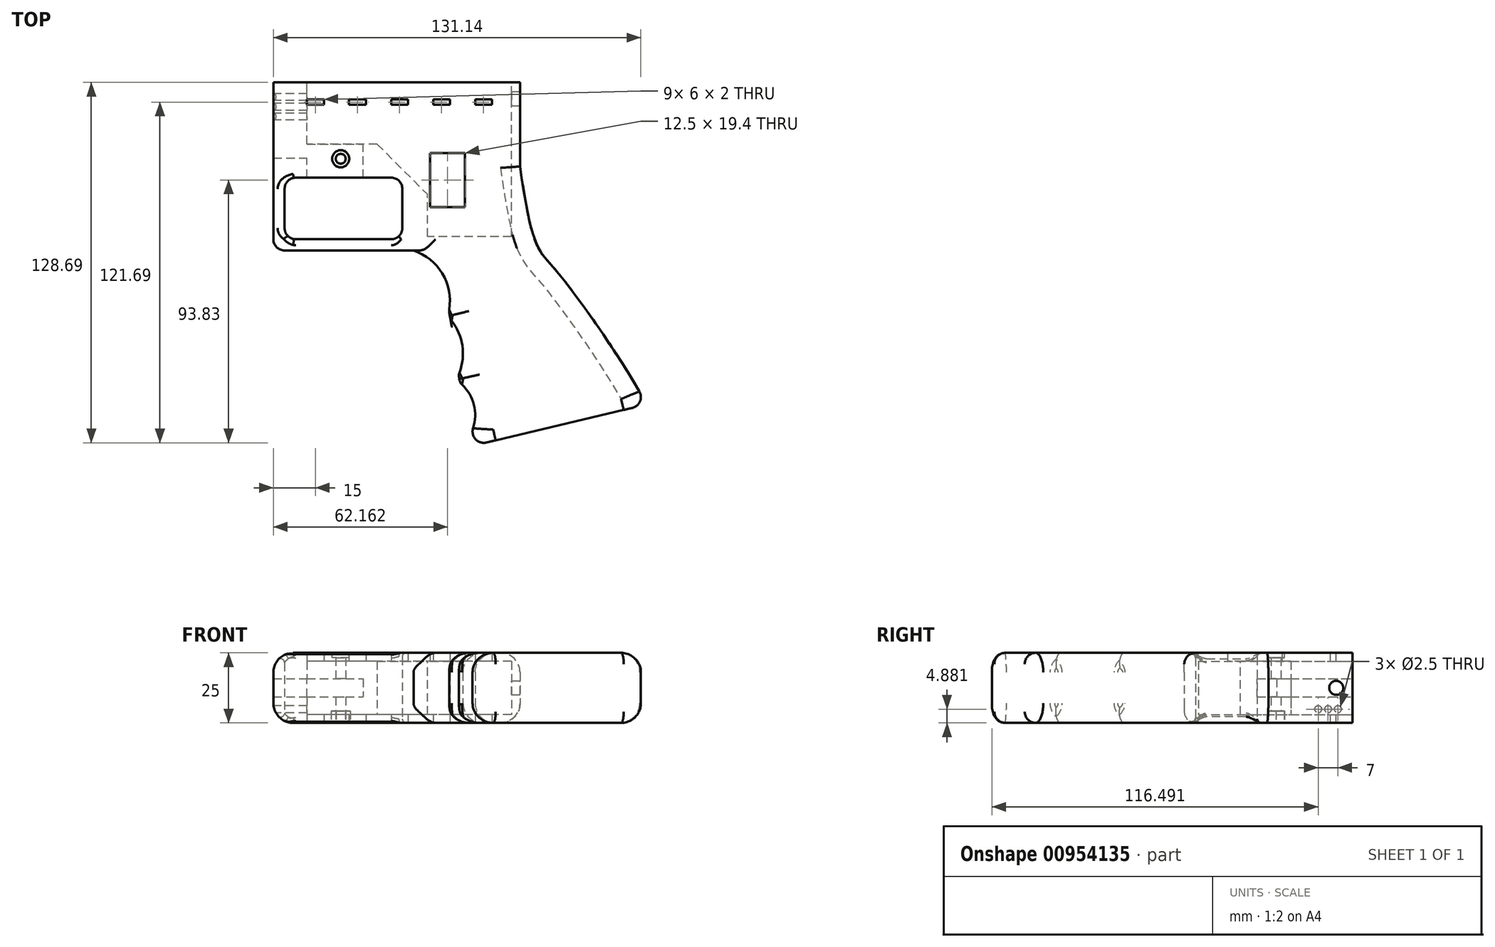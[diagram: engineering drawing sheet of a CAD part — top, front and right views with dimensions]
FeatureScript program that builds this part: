
annotation { "Feature Type Name" : "Feature", "Feature Type Description" : "" }
export const myFeature = defineFeature(function(context is Context, id is Id, definition is map)
    precondition{}
    {
        {
            var Q0;
            Q0=qCreatedBy(makeId("Top.planeOp"),FACE);
            var sketch = newSketch(context, id + "F0", { "sketchPlane" : qUnion([Q0])});
            skLineSegment(sketch, "E0.bottom", {"start": v(44, 30) * mm, "end": v(-44, 30) * mm});
            skLineSegment(sketch, "E0.top", {"start": v(44, -30) * mm, "end": v(-44, -30) * mm});
            skLineSegment(sketch, "E0.left", {"start": v(44, 30) * mm, "end": v(44, -30) * mm});
            skLineSegment(sketch, "E0.right", {"start": v(-44, 30) * mm, "end": v(-44, -30) * mm});
            skPoint(sketch, "E0.middle", {"position": v(0, 0) * mm});
            skLineSegment(sketch, "E1.bottom", {"start": v(-40, -4) * mm, "end": v(2, -4) * mm});
            skLineSegment(sketch, "E1.top", {"start": v(-40, -26) * mm, "end": v(2, -26) * mm});
            skLineSegment(sketch, "E1.left", {"start": v(-40, -4) * mm, "end": v(-40, -26) * mm});
            skLineSegment(sketch, "E1.right", {"start": v(2, -4) * mm, "end": v(2, -26) * mm});
            skLineSegment(sketch, "E2.bottom", {"start": v(-32, 24) * mm, "end": v(-26, 24) * mm});
            skLineSegment(sketch, "E2.top", {"start": v(-32, 22) * mm, "end": v(-26, 22) * mm});
            skLineSegment(sketch, "E2.left", {"start": v(-32, 24) * mm, "end": v(-32, 22) * mm});
            skLineSegment(sketch, "E2.right", {"start": v(-26, 24) * mm, "end": v(-26, 22) * mm});
            skLineSegment(sketch, "E3.1.0.0", {"start": v(-17, 24) * mm, "end": v(-11, 24) * mm});
            skLineSegment(sketch, "E3.1.0.1", {"start": v(-11, 24) * mm, "end": v(-11, 22) * mm});
            skLineSegment(sketch, "E3.1.0.2", {"start": v(-17, 22) * mm, "end": v(-11, 22) * mm});
            skLineSegment(sketch, "E3.1.0.3", {"start": v(-17, 24) * mm, "end": v(-17, 22) * mm});
            skLineSegment(sketch, "E3.2.0.0", {"start": v(-2, 24) * mm, "end": v(4, 24) * mm});
            skLineSegment(sketch, "E3.2.0.1", {"start": v(4, 24) * mm, "end": v(4, 22) * mm});
            skLineSegment(sketch, "E3.2.0.2", {"start": v(-2, 22) * mm, "end": v(4, 22) * mm});
            skLineSegment(sketch, "E3.2.0.3", {"start": v(-2, 24) * mm, "end": v(-2, 22) * mm});
            skLineSegment(sketch, "E3.direction1", {"start": v(-32, 24) * mm, "end": v(-17, 24) * mm, "construction": true});
            skLineSegment(sketch, "E4.0.3.0", {"start": v(13, 24) * mm, "end": v(19, 24) * mm});
            skLineSegment(sketch, "E4.3.3.0", {"start": v(19, 24) * mm, "end": v(19, 22) * mm});
            skLineSegment(sketch, "E4.6.3.0", {"start": v(13, 22) * mm, "end": v(19, 22) * mm});
            skLineSegment(sketch, "E4.9.3.0", {"start": v(13, 24) * mm, "end": v(13, 22) * mm});
            skLineSegment(sketch, "E4.0.4.0", {"start": v(28, 24) * mm, "end": v(34, 24) * mm});
            skLineSegment(sketch, "E4.3.4.0", {"start": v(34, 24) * mm, "end": v(34, 22) * mm});
            skLineSegment(sketch, "E4.6.4.0", {"start": v(28, 22) * mm, "end": v(34, 22) * mm});
            skLineSegment(sketch, "E4.9.4.0", {"start": v(28, 24) * mm, "end": v(28, 22) * mm});
            skFitSpline(sketch, "E5", {"points": [v(44, 0) * mm, v(56.7, -36.96) * mm, v(89.25, -85) * mm], "startDerivative": vector(29.34, -199.67) * mm, "endDerivative": vector(48.39, -88.32) * mm});
            skLineSegment(sketch, "E6", {"start": v(89.25, -85) * mm, "end": v(26, -100) * mm});
            skLineSegment(sketch, "E7", {"start": v(26, -100) * mm, "end": v(25.55, -97.03) * mm});
            skArc(sketch, "E8", {"start": v(18.67, -51.55) * mm, "mid": v(16.38, -38.4) * mm, "end": v(6, -30) * mm});
            skArc(sketch, "E9", {"start": v(22.11, -74.3) * mm, "mid": v(23.43, -63.98) * mm, "end": v(19.12, -54.52) * mm});
            skArc(sketch, "E10", {"start": v(25.55, -97.03) * mm, "mid": v(27.83, -86.57) * mm, "end": v(22.56, -77.26) * mm});
            skLineSegment(sketch, "E11.trimOffspring", {"start": v(19.12, -54.52) * mm, "end": v(18.67, -51.55) * mm});
            skLineSegment(sketch, "E12.trimOffspring", {"start": v(22.56, -77.26) * mm, "end": v(22.11, -74.3) * mm});
            skSolve(sketch);
        }
        {
            var Q0;
            {var subQ1=sQuery(id+"F0.wireOp",EDGE,"E0.bottom");Q0=makeQuery(id+"F0.imprint","IMPRINT",FACE,{"disambiguationData":[TD([[makeQuery(id+"F0.imprint","IMPRINT",EDGE,{"derivedFrom":subQ1}),1.0]])]});}
            var Q1;
            {var subQ0=sQuery(id+"F0.wireOp",EDGE,"E5");Q1=makeQuery(id+"F0.imprint","IMPRINT",FACE,{"disambiguationData":[TD([[makeQuery(id+"F0.imprint","IMPRINT",EDGE,{"derivedFrom":subQ0}),-1.0]])]});}
            extrude(context, id + "F1", {"entities" : qUnion([Q0, Q1]), "depth" : 25 * mm, "offsetDistance" : 25 * mm});
        }
        {
            var Q0;
            Q0=makeQuery(id+"F1.opExtrude","SWEPT_FACE",FACE,{"disambiguationData":[OSD([sQuery(id+"F0.wireOp",EDGE,"E0.bottom")])]});
            var sketch = newSketch(context, id + "F2", { "sketchPlane" : qUnion([Q0])});
            skLineSegment(sketch, "E13.bottom", {"start": v(-41, 22) * mm, "end": v(32, 22) * mm});
            skLineSegment(sketch, "E13.top", {"start": v(-41, 3) * mm, "end": v(32, 3) * mm});
            skLineSegment(sketch, "E13.left", {"start": v(-41, 22) * mm, "end": v(-41, 3) * mm});
            skLineSegment(sketch, "E13.right", {"start": v(32, 22) * mm, "end": v(32, 3) * mm});
            skLineSegment(sketch, "E14", {"start": v(-11, 22) * mm, "end": v(-11, 3) * mm});
            skLineSegment(sketch, "E15.bottom", {"start": v(44, 15.75) * mm, "end": v(12, 15.75) * mm});
            skLineSegment(sketch, "E15.top", {"start": v(44, 9.25) * mm, "end": v(12, 9.25) * mm});
            skLineSegment(sketch, "E15.left", {"start": v(44, 15.75) * mm, "end": v(44, 9.25) * mm});
            skLineSegment(sketch, "E15.right", {"start": v(12, 15.75) * mm, "end": v(12, 9.25) * mm});
            skLineSegment(sketch, "E16", {"start": v(16.73, 22) * mm, "end": v(16.73, 15.75) * mm, "construction": true});
            skLineSegment(sketch, "E17", {"start": v(16.98, 9.25) * mm, "end": v(16.98, 3) * mm, "construction": true});
            skSolve(sketch);
        }
        {
            var Q0;
            {var subQ0=sQuery(id+"F2.wireOp",EDGE,"E13.left");Q0=makeQuery(id+"F2.imprint","IMPRINT",FACE,{"disambiguationData":[TD([[makeQuery(id+"F2.imprint","IMPRINT",EDGE,{"derivedFrom":subQ0}),1.0]])]});}
            var Q1;
            {var subQ9=sQuery(id+"F2.wireOp",EDGE,"E14");Q1=makeQuery(id+"F2.imprint","IMPRINT",FACE,{"disambiguationData":[TD([[makeQuery(id+"F2.imprint","IMPRINT",EDGE,{"derivedFrom":subQ9}),1.0]])]});}
            var Q2;
            {var subQ5=sQuery(id+"F2.wireOp",EDGE,"E15.left");Q2=makeQuery(id+"F2.imprint","IMPRINT",FACE,{"disambiguationData":[TD([[makeQuery(id+"F2.imprint","IMPRINT",EDGE,{"derivedFrom":subQ5}),-1.0]])]});}
            var Q3;
            {var subQ5=sQuery(id+"F2.wireOp",EDGE,"E15.right");Q3=makeQuery(id+"F2.imprint","IMPRINT",FACE,{"disambiguationData":[TD([[makeQuery(id+"F2.imprint","IMPRINT",EDGE,{"derivedFrom":subQ5}),1.0]])]});}
            extrude(context, id + "F3", {"entities" : qUnion([Q0, Q1, Q2, Q3]), "operationType" : NewBodyOperationType.REMOVE, "oppositeDirection" : true, "depth" : 22 * mm, "offsetDistance" : 25 * mm});
        }
        {
            var Q0;
            {var subQ0=sQuery(id+"F2.wireOp",EDGE,"E13.left");Q0=makeQuery(id+"F2.imprint","IMPRINT",FACE,{"disambiguationData":[TD([[makeQuery(id+"F2.imprint","IMPRINT",EDGE,{"derivedFrom":subQ0}),1.0]])]});}
            extrude(context, id + "F4", {"entities" : qUnion([Q0]), "operationType" : NewBodyOperationType.REMOVE, "oppositeDirection" : true, "depth" : 55 * mm, "offsetDistance" : 25 * mm});
        }
        {
            var Q0;
            {var subQ5=sQuery(id+"F2.wireOp",EDGE,"E15.right");Q0=makeQuery(id+"F2.imprint","IMPRINT",FACE,{"disambiguationData":[TD([[makeQuery(id+"F2.imprint","IMPRINT",EDGE,{"derivedFrom":subQ5}),1.0]])]});}
            var Q1;
            Q1=makeQuery(id+"F1.opExtrude","SWEPT_FACE",FACE,{"disambiguationData":[OSD([sQuery(id+"F0.wireOp",EDGE,"E1.bottom")])]});
            extrude(context, id + "F5", {"entities" : qUnion([Q0]), "operationType" : NewBodyOperationType.REMOVE, "endBound" : BoundingType.UP_TO_SURFACE, "oppositeDirection" : true, "depth" : 25 * mm, "endBoundEntityFace" : qUnion([Q1]), "offsetDistance" : 25 * mm});
        }
        {
            var Q0;
            {var subQ5=sQuery(id+"F2.wireOp",EDGE,"E15.left");Q0=makeQuery(id+"F2.imprint","IMPRINT",FACE,{"disambiguationData":[TD([[makeQuery(id+"F2.imprint","IMPRINT",EDGE,{"derivedFrom":subQ5}),-1.0]])]});}
            extrude(context, id + "F6", {"entities" : qUnion([Q0]), "operationType" : NewBodyOperationType.REMOVE, "oppositeDirection" : true, "depth" : 27 * mm, "offsetDistance" : 25 * mm});
        }
        {
            var Q0;
            Q0=makeQuery(id+"F1.opExtrude","CAP_FACE",FACE,{"disambiguationData":[OSD([sQuery(id+"F0.wireOp",EDGE,"E0.bottom"),sQuery(id+"F0.wireOp",EDGE,"E0.top"),sQuery(id+"F0.wireOp",EDGE,"E0.left"),sQuery(id+"F0.wireOp",EDGE,"E0.right"),sQuery(id+"F0.wireOp",EDGE,"E1.bottom"),sQuery(id+"F0.wireOp",EDGE,"E1.top"),sQuery(id+"F0.wireOp",EDGE,"E1.left"),sQuery(id+"F0.wireOp",EDGE,"E1.right"),sQuery(id+"F0.wireOp",EDGE,"E2.bottom"),sQuery(id+"F0.wireOp",EDGE,"E2.top"),sQuery(id+"F0.wireOp",EDGE,"E2.left"),sQuery(id+"F0.wireOp",EDGE,"E2.right"),sQuery(id+"F0.wireOp",EDGE,"E3.1.0.0"),sQuery(id+"F0.wireOp",EDGE,"E3.1.0.1"),sQuery(id+"F0.wireOp",EDGE,"E3.1.0.2"),sQuery(id+"F0.wireOp",EDGE,"E3.1.0.3"),sQuery(id+"F0.wireOp",EDGE,"E3.2.0.0"),sQuery(id+"F0.wireOp",EDGE,"E3.2.0.1"),sQuery(id+"F0.wireOp",EDGE,"E3.2.0.2"),sQuery(id+"F0.wireOp",EDGE,"E3.2.0.3"),sQuery(id+"F0.wireOp",EDGE,"E4.0.3.0"),sQuery(id+"F0.wireOp",EDGE,"E4.3.3.0"),sQuery(id+"F0.wireOp",EDGE,"E4.6.3.0"),sQuery(id+"F0.wireOp",EDGE,"E4.9.3.0"),sQuery(id+"F0.wireOp",EDGE,"E4.0.4.0"),sQuery(id+"F0.wireOp",EDGE,"E4.3.4.0"),sQuery(id+"F0.wireOp",EDGE,"E4.6.4.0"),sQuery(id+"F0.wireOp",EDGE,"E4.9.4.0"),sQuery(id+"F0.wireOp",EDGE,"E5"),sQuery(id+"F0.wireOp",EDGE,"E6"),sQuery(id+"F0.wireOp",EDGE,"E7"),sQuery(id+"F0.wireOp",EDGE,"E8"),sQuery(id+"F0.wireOp",EDGE,"E9"),sQuery(id+"F0.wireOp",EDGE,"E10"),sQuery(id+"F0.wireOp",EDGE,"E11.trimOffspring"),sQuery(id+"F0.wireOp",EDGE,"E12.trimOffspring")])],"isStart":true});
            var sketch = newSketch(context, id + "F7", { "sketchPlane" : qUnion([Q0])});
            skCircle(sketch, "E18", {"center": v(-19.98, -2.75) * mm, "radius": 1.75 * mm});
            skLineSegment(sketch, "E19.bottom", {"start": v(11.91, -4.84) * mm, "end": v(24.41, -4.84) * mm});
            skLineSegment(sketch, "E19.top", {"start": v(11.91, 14.56) * mm, "end": v(24.41, 14.56) * mm});
            skLineSegment(sketch, "E19.left", {"start": v(11.91, -4.84) * mm, "end": v(11.91, 14.56) * mm});
            skLineSegment(sketch, "E19.right", {"start": v(24.41, -4.84) * mm, "end": v(24.41, 14.56) * mm});
            skSolve(sketch);
        }
        {
            var Q0;
            Q0=makeQuery(id+"F4.boolean.opBoolean","INTERSECT",EDGE,{"derivedFrom":[makeQuery(id+"F3.boolean.opBoolean","COPY",FACE,{"derivedFrom":makeQuery(id+"F3.opExtrude","CAP_FACE",FACE,{"disambiguationData":[OSD([sQuery(id+"F2.wireOp",EDGE,"E13.bottom"),sQuery(id+"F2.wireOp",EDGE,"E13.top"),sQuery(id+"F2.wireOp",EDGE,"E13.left"),sQuery(id+"F2.wireOp",EDGE,"E13.right"),sQuery(id+"F2.wireOp",EDGE,"E15.bottom"),sQuery(id+"F2.wireOp",EDGE,"E15.top"),sQuery(id+"F2.wireOp",EDGE,"E15.left")])],"isStart":false})}),makeQuery(id+"F4.opExtrude","SWEPT_FACE",FACE,{"disambiguationData":[OSD([sQuery(id+"F2.wireOp",EDGE,"E14")])]})]});
            chamfer(context, id + "F8", {"entities" : qUnion([Q0]), "width" : 18 * mm, "tangentPropagation" : true});
        }
        {
            var Q0;
            Q0=makeQuery(id+"F7.imprint","IMPRINT",FACE,{"disambiguationData":[TD([[makeQuery(id+"F7.imprint","IMPRINT",EDGE,{"derivedFrom":sQuery(id+"F7.wireOp",EDGE,"E19.bottom")}),1.0]])]});
            extrude(context, id + "F9", {"entities" : qUnion([Q0]), "operationType" : NewBodyOperationType.REMOVE, "oppositeDirection" : true, "depth" : 41.3 * mm, "offsetDistance" : 25 * mm, "hasSecondDirection" : true, "secondDirectionOppositeDirection" : true, "secondDirectionDepth" : 12.7 * mm});
        }
        {
            var Q0;
            Q0=makeQuery(id+"F7.imprint","IMPRINT",FACE,{"disambiguationData":[TD([[makeQuery(id+"F7.imprint","IMPRINT",EDGE,{"derivedFrom":sQuery(id+"F7.wireOp",EDGE,"E18")}),1.0]])]});
            extrude(context, id + "F10", {"entities" : qUnion([Q0]), "operationType" : NewBodyOperationType.REMOVE, "oppositeDirection" : true, "depth" : 25 * mm, "offsetDistance" : 25 * mm, "hasSecondDirection" : true, "secondDirectionOppositeDirection" : false, "secondDirectionDepth" : 13.3 * mm});
        }
        {
            var Q0;
            Q0=makeQuery(id+"F1.opExtrude","CAP_EDGE",EDGE,{"disambiguationData":[OSD([sQuery(id+"F0.wireOp",EDGE,"E5")])],"isStart":true});
            var Q1;
            Q1=makeQuery(id+"F1.opExtrude","CAP_EDGE",EDGE,{"disambiguationData":[OSD([sQuery(id+"F0.wireOp",EDGE,"E5")])],"isStart":false});
            var Q2;
            Q2=makeQuery(id+"F1.opExtrude","CAP_EDGE",EDGE,{"disambiguationData":[OSD([sQuery(id+"F0.wireOp",EDGE,"E0.left")])],"isStart":false});
            var Q3;
            Q3=makeQuery(id+"F1.opExtrude","CAP_EDGE",EDGE,{"disambiguationData":[OSD([sQuery(id+"F0.wireOp",EDGE,"E0.left")])],"isStart":true});
            var Q4;
            Q4=makeQuery(id+"F1.opExtrude","CAP_EDGE",EDGE,{"disambiguationData":[OSD([sQuery(id+"F0.wireOp",EDGE,"E8")])],"isStart":false});
            var Q5;
            Q5=makeQuery(id+"F1.opExtrude","CAP_EDGE",EDGE,{"disambiguationData":[OSD([sQuery(id+"F0.wireOp",EDGE,"E8")])],"isStart":true});
            var Q6;
            Q6=makeQuery(id+"F1.opExtrude","CAP_EDGE",EDGE,{"disambiguationData":[OSD([sQuery(id+"F0.wireOp",EDGE,"E9")])],"isStart":true});
            var Q7;
            Q7=makeQuery(id+"F1.opExtrude","CAP_EDGE",EDGE,{"disambiguationData":[OSD([sQuery(id+"F0.wireOp",EDGE,"E9")])],"isStart":false});
            var Q8;
            Q8=makeQuery(id+"F1.opExtrude","CAP_EDGE",EDGE,{"disambiguationData":[OSD([sQuery(id+"F0.wireOp",EDGE,"E10")])],"isStart":false});
            var Q9;
            Q9=makeQuery(id+"F1.opExtrude","CAP_EDGE",EDGE,{"disambiguationData":[OSD([sQuery(id+"F0.wireOp",EDGE,"E10")])],"isStart":true});
            var Q10;
            Q10=makeQuery(id+"F1.opExtrude","CAP_EDGE",EDGE,{"disambiguationData":[OSD([sQuery(id+"F0.wireOp",EDGE,"E0.right")])],"isStart":false});
            var Q11;
            Q11=makeQuery(id+"F1.opExtrude","CAP_EDGE",EDGE,{"disambiguationData":[OSD([sQuery(id+"F0.wireOp",EDGE,"E0.right")])],"isStart":true});
            fillet(context, id + "F11", {"entities" : qUnion([Q0, Q1, Q2, Q3, Q4, Q5, Q6, Q7, Q8, Q9, Q10, Q11]), "radius" : 7 * mm, "tangentPropagation" : true, "allowEdgeOverflow" : false});
        }
        {
            var Q0;
            Q0=makeQuery(id+"F1.opExtrude","SWEPT_EDGE",EDGE,{"disambiguationData":[OSD([sQuery(id+"F0.wireOp",EDGE,"E1.top"),sQuery(id+"F0.wireOp",EDGE,"E1.left")])]});
            var Q1;
            Q1=makeQuery(id+"F1.opExtrude","SWEPT_EDGE",EDGE,{"disambiguationData":[OSD([sQuery(id+"F0.wireOp",EDGE,"E1.bottom"),sQuery(id+"F0.wireOp",EDGE,"E1.left")])]});
            var Q2;
            Q2=makeQuery(id+"F1.opExtrude","SWEPT_EDGE",EDGE,{"disambiguationData":[OSD([sQuery(id+"F0.wireOp",EDGE,"E1.bottom"),sQuery(id+"F0.wireOp",EDGE,"E1.right")])]});
            var Q3;
            Q3=makeQuery(id+"F1.opExtrude","SWEPT_EDGE",EDGE,{"disambiguationData":[OSD([sQuery(id+"F0.wireOp",EDGE,"E1.top"),sQuery(id+"F0.wireOp",EDGE,"E1.right")])]});
            fillet(context, id + "F12", {"entities" : qUnion([Q0, Q1, Q2, Q3]), "radius" : 4 * mm, "tangentPropagation" : true, "allowEdgeOverflow" : false});
        }
        {
            var Q0;
            Q0=makeQuery(id+"F1.opExtrude","CAP_EDGE",EDGE,{"disambiguationData":[OSD([sQuery(id+"F0.wireOp",EDGE,"E0.top")])],"isStart":true});
            var Q1;
            Q1=makeQuery(id+"F1.opExtrude","CAP_EDGE",EDGE,{"disambiguationData":[OSD([sQuery(id+"F0.wireOp",EDGE,"E6")])],"isStart":false});
            var Q2;
            Q2=makeQuery(id+"F1.opExtrude","SWEPT_EDGE",EDGE,{"disambiguationData":[OSD([sQuery(id+"F0.wireOp",EDGE,"E6"),sQuery(id+"F0.wireOp",EDGE,"E7")])]});
            fillet(context, id + "F13", {"entities" : qUnion([Q0, Q1, Q2]), "radius" : 4 * mm, "tangentPropagation" : true, "allowEdgeOverflow" : false});
        }
        {
            var Q0;
            Q0=makeQuery(id+"F1.opExtrude","SWEPT_FACE",FACE,{"disambiguationData":[OSD([sQuery(id+"F0.wireOp",EDGE,"E11.trimOffspring")])]});
            var Q1;
            Q1=makeQuery(id+"F1.opExtrude","SWEPT_FACE",FACE,{"disambiguationData":[OSD([sQuery(id+"F0.wireOp",EDGE,"E12.trimOffspring")])]});
            fillet(context, id + "F14", {"entities" : qUnion([Q0, Q1]), "radius" : 3 * mm, "tangentPropagation" : true, "allowEdgeOverflow" : false});
        }
        {
            var Q0;
            Q0=makeQuery(id+"F1.opExtrude","CAP_EDGE",EDGE,{"disambiguationData":[OSD([sQuery(id+"F0.wireOp",EDGE,"E1.right")])],"isStart":false});
            var Q1;
            Q1=makeQuery(id+"F1.opExtrude","CAP_EDGE",EDGE,{"disambiguationData":[OSD([sQuery(id+"F0.wireOp",EDGE,"E1.bottom")])],"isStart":false});
            var Q2;
            Q2=makeQuery(id+"F1.opExtrude","CAP_EDGE",EDGE,{"disambiguationData":[OSD([sQuery(id+"F0.wireOp",EDGE,"E1.bottom")])],"isStart":true});
            fillet(context, id + "F15", {"entities" : qUnion([Q0, Q1, Q2]), "radius" : 1.4 * mm, "tangentPropagation" : true, "allowEdgeOverflow" : false});
        }
        {
            var Q0;
            Q0=makeQuery(id+"F1.opExtrude","SWEPT_FACE",FACE,{"disambiguationData":[OSD([sQuery(id+"F0.wireOp",EDGE,"E0.right")])]});
            var sketch = newSketch(context, id + "F16", { "sketchPlane" : qUnion([Q0])});
            skCircle(sketch, "E20", {"center": v(-24.8, 4.88) * mm, "radius": 1.25 * mm});
            skCircle(sketch, "E21.1.0.0", {"center": v(-21.3, 4.88) * mm, "radius": 1.25 * mm});
            skCircle(sketch, "E21.2.0.0", {"center": v(-17.8, 4.88) * mm, "radius": 1.25 * mm});
            skLineSegment(sketch, "E21.direction1", {"start": v(-24.8, 4.88) * mm, "end": v(-21.3, 4.88) * mm, "construction": true});
            skSolve(sketch);
        }
        {
            var Q0;
            Q0=makeQuery(id+"F16.imprint","IMPRINT",FACE,{"disambiguationData":[TD([[makeQuery(id+"F16.imprint","IMPRINT",EDGE,{"derivedFrom":sQuery(id+"F16.wireOp",EDGE,"E20")}),1.0]])]});
            var Q1;
            Q1=makeQuery(id+"F16.imprint","IMPRINT",FACE,{"disambiguationData":[TD([[makeQuery(id+"F16.imprint","IMPRINT",EDGE,{"derivedFrom":sQuery(id+"F16.wireOp",EDGE,"E21.1.0.0")}),1.0]])]});
            var Q2;
            Q2=makeQuery(id+"F16.imprint","IMPRINT",FACE,{"disambiguationData":[TD([[makeQuery(id+"F16.imprint","IMPRINT",EDGE,{"derivedFrom":sQuery(id+"F16.wireOp",EDGE,"E21.2.0.0")}),1.0]])]});
            extrude(context, id + "F17", {"entities" : qUnion([Q0, Q1, Q2]), "operationType" : NewBodyOperationType.REMOVE, "oppositeDirection" : true, "depth" : 13.3 * mm, "offsetDistance" : 25 * mm});
        }
        {
            var Q0;
            Q0=makeQuery(id+"F13.opFillet","SPLIT",FACE,{"disambiguationData":[OD(0.0)],"derivedFrom":makeQuery(id+"F1.opExtrude","CAP_FACE",FACE,{"disambiguationData":[OSD([sQuery(id+"F0.wireOp",EDGE,"E0.bottom"),sQuery(id+"F0.wireOp",EDGE,"E0.top"),sQuery(id+"F0.wireOp",EDGE,"E0.left"),sQuery(id+"F0.wireOp",EDGE,"E0.right"),sQuery(id+"F0.wireOp",EDGE,"E1.bottom"),sQuery(id+"F0.wireOp",EDGE,"E1.top"),sQuery(id+"F0.wireOp",EDGE,"E1.left"),sQuery(id+"F0.wireOp",EDGE,"E1.right"),sQuery(id+"F0.wireOp",EDGE,"E2.bottom"),sQuery(id+"F0.wireOp",EDGE,"E2.top"),sQuery(id+"F0.wireOp",EDGE,"E2.left"),sQuery(id+"F0.wireOp",EDGE,"E2.right"),sQuery(id+"F0.wireOp",EDGE,"E3.1.0.0"),sQuery(id+"F0.wireOp",EDGE,"E3.1.0.1"),sQuery(id+"F0.wireOp",EDGE,"E3.1.0.2"),sQuery(id+"F0.wireOp",EDGE,"E3.1.0.3"),sQuery(id+"F0.wireOp",EDGE,"E3.2.0.0"),sQuery(id+"F0.wireOp",EDGE,"E3.2.0.1"),sQuery(id+"F0.wireOp",EDGE,"E3.2.0.2"),sQuery(id+"F0.wireOp",EDGE,"E3.2.0.3"),sQuery(id+"F0.wireOp",EDGE,"E4.0.3.0"),sQuery(id+"F0.wireOp",EDGE,"E4.3.3.0"),sQuery(id+"F0.wireOp",EDGE,"E4.6.3.0"),sQuery(id+"F0.wireOp",EDGE,"E4.9.3.0"),sQuery(id+"F0.wireOp",EDGE,"E4.0.4.0"),sQuery(id+"F0.wireOp",EDGE,"E4.3.4.0"),sQuery(id+"F0.wireOp",EDGE,"E4.6.4.0"),sQuery(id+"F0.wireOp",EDGE,"E4.9.4.0"),sQuery(id+"F0.wireOp",EDGE,"E5"),sQuery(id+"F0.wireOp",EDGE,"E6"),sQuery(id+"F0.wireOp",EDGE,"E7"),sQuery(id+"F0.wireOp",EDGE,"E8"),sQuery(id+"F0.wireOp",EDGE,"E9"),sQuery(id+"F0.wireOp",EDGE,"E10"),sQuery(id+"F0.wireOp",EDGE,"E11.trimOffspring"),sQuery(id+"F0.wireOp",EDGE,"E12.trimOffspring")])],"isStart":false})});
            var sketch = newSketch(context, id + "F18", { "sketchPlane" : qUnion([Q0])});
            skCircle(sketch, "E22", {"center": v(-19.98, 2.75) * mm, "radius": 3.05 * mm});
            skSolve(sketch);
        }
        {
            var Q0;
            Q0=makeQuery(id+"F18.imprint","IMPRINT",FACE,{"disambiguationData":[TD([[makeQuery(id+"F18.imprint","IMPRINT",EDGE,{"derivedFrom":sQuery(id+"F18.wireOp",EDGE,"E22")}),1.0]])]});
            extrude(context, id + "F19", {"entities" : qUnion([Q0]), "operationType" : NewBodyOperationType.REMOVE, "oppositeDirection" : true, "depth" : 1.7 * mm, "offsetDistance" : 25 * mm});
        }
        {
            var Q0;
            Q0=makeQuery(id+"F7.imprint","IMPRINT",FACE,{"disambiguationData":[TD([[makeQuery(id+"F7.imprint","IMPRINT",EDGE,{"derivedFrom":sQuery(id+"F7.wireOp",EDGE,"E18")}),-1.0]])]});
            var sketch = newSketch(context, id + "F20", { "sketchPlane" : qUnion([Q0])});
            skLineSegment(sketch, "E23.0", {"start": v(-23.39, -2.77) * mm, "end": v(-21.7, 0.19) * mm});
            skLineSegment(sketch, "E23.1", {"start": v(-21.7, 0.19) * mm, "end": v(-18.3, 0.22) * mm});
            skLineSegment(sketch, "E23.2", {"start": v(-18.3, 0.22) * mm, "end": v(-16.57, -2.72) * mm});
            skLineSegment(sketch, "E23.3", {"start": v(-16.57, -2.72) * mm, "end": v(-18.25, -5.68) * mm});
            skLineSegment(sketch, "E23.4", {"start": v(-18.25, -5.68) * mm, "end": v(-21.66, -5.71) * mm});
            skLineSegment(sketch, "E23.5", {"start": v(-21.66, -5.71) * mm, "end": v(-23.39, -2.77) * mm});
            skPoint(sketch, "E23.0.midPoint", {"position": v(-22.55, -1.3) * mm});
            skSolve(sketch);
        }
        {
            var Q0;
            Q0=makeQuery(id+"F20.imprint","IMPRINT",FACE,{"disambiguationData":[TD([[makeQuery(id+"F20.imprint","IMPRINT",EDGE,{"derivedFrom":sQuery(id+"F20.wireOp",EDGE,"E23.0")}),-1.0]])]});
            var Q1;
            Q1=sQuery(id+"F20.wireOp",EDGE,"E23.5");
            var Q2;
            Q2=sQuery(id+"F20.wireOp",EDGE,"E23.1");
            var Q3;
            Q3=sQuery(id+"F20.wireOp",EDGE,"E23.2");
            var Q4;
            Q4=sQuery(id+"F20.wireOp",EDGE,"E23.3");
            var Q5;
            Q5=sQuery(id+"F20.wireOp",EDGE,"E23.4");
            var Q6;
            Q6=sQuery(id+"F20.wireOp",EDGE,"E23.0");
            extrude(context, id + "F21", {"entities" : qUnion([Q0]), "operationType" : NewBodyOperationType.REMOVE, "surfaceEntities" : qUnion([Q1, Q2, Q3, Q4, Q5, Q6]), "oppositeDirection" : true, "depth" : 4.2 * mm, "offsetDistance" : 25 * mm});
        }
        {
            var Q0;
            Q0=makeQuery(id+"F1.opExtrude","SWEPT_FACE",FACE,{"disambiguationData":[OSD([sQuery(id+"F0.wireOp",EDGE,"E0.left")])]});
            var sketch = newSketch(context, id + "F22", { "sketchPlane" : qUnion([Q0])});
            skCircle(sketch, "E24", {"center": v(24.22, 12.5) * mm, "radius": 2.5 * mm});
            skPoint(sketch, "E24.centerSnap0", {"position": v(0, 12.5) * mm});
            skSolve(sketch);
        }
        {
            var Q0;
            Q0=makeQuery(id+"F22.imprint","IMPRINT",FACE,{"disambiguationData":[TD([[makeQuery(id+"F22.imprint","IMPRINT",EDGE,{"derivedFrom":sQuery(id+"F22.wireOp",EDGE,"E24")}),1.0]])]});
            extrude(context, id + "F23", {"entities" : qUnion([Q0]), "operationType" : NewBodyOperationType.REMOVE, "oppositeDirection" : true, "depth" : 4 * mm, "offsetDistance" : 25 * mm});
        }
    });
